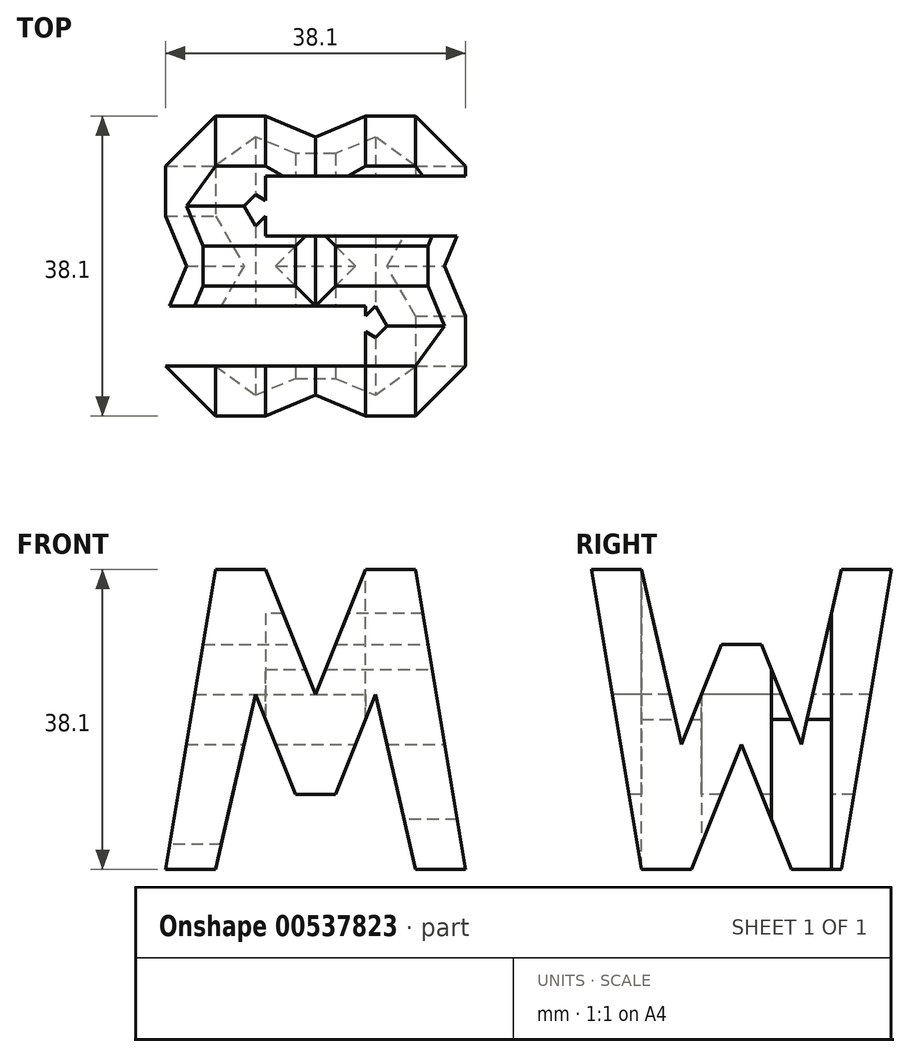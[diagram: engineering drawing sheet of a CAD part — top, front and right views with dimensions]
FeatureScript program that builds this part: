
annotation { "Feature Type Name" : "Feature", "Feature Type Description" : "" }
export const myFeature = defineFeature(function(context is Context, id is Id, definition is map)
    precondition{}
    {
        {
            var Q0;
            Q0=qCreatedBy(makeId("Front.planeOp"),FACE);
            var sketch = newSketch(context, id + "F0", { "sketchPlane" : qUnion([Q0])});
            skLineSegment(sketch, "E0", {"start": v(0, 0) * mm, "end": v(0, 38.1) * mm});
            skLineSegment(sketch, "E1", {"start": v(0, 38.1) * mm, "end": v(38.1, 38.1) * mm});
            skLineSegment(sketch, "E2", {"start": v(38.1, 38.1) * mm, "end": v(38.1, 0) * mm});
            skLineSegment(sketch, "E3", {"start": v(38.1, 0) * mm, "end": v(0, 0) * mm});
            skSolve(sketch);
        }
        {
            var Q0;
            Q0 = qSketchRegion(id + "F0", true);
            extrude(context, id + "F1", {"entities" : qUnion([Q0]), "depth" : 38.1 * mm, "offsetDistance" : 25.4 * mm});
        }
        {
            var Q0;
            Q0=qCreatedBy(makeId("Front.planeOp"),FACE);
            cPlane(context, id + "F2", {"entities" : qUnion([Q0]), "cplaneType" : CPlaneType.OFFSET, "offset" : 38.1 * mm, "width" : 152.4 * mm, "height" : 152.4 * mm});
        }
        {
            var Q0;
            Q0=qCreatedBy(makeId("Right.planeOp"),FACE);
            cPlane(context, id + "F3", {"entities" : qUnion([Q0]), "cplaneType" : CPlaneType.OFFSET, "offset" : 38.1 * mm, "width" : 152.4 * mm, "height" : 152.4 * mm});
        }
        {
            var Q0;
            Q0=qCreatedBy(makeId("Top.planeOp"),FACE);
            cPlane(context, id + "F4", {"entities" : qUnion([Q0]), "cplaneType" : CPlaneType.OFFSET, "offset" : 38.1 * mm, "width" : 152.4 * mm, "height" : 152.4 * mm});
        }
        {
            var Q0;
            Q0=qCreatedBy(id+"F3.planeOp",FACE);
            var sketch = newSketch(context, id + "F5", { "sketchPlane" : qUnion([Q0])});
            skLineSegment(sketch, "E4.bottom", {"start": v(0, 0) * mm, "end": v(-38.1, 0) * mm});
            skLineSegment(sketch, "E4.top", {"start": v(0, 38.1) * mm, "end": v(-38.1, 38.1) * mm});
            skLineSegment(sketch, "E4.left", {"start": v(0, 0) * mm, "end": v(0, 38.1) * mm});
            skLineSegment(sketch, "E4.right", {"start": v(-38.1, 0) * mm, "end": v(-38.1, 38.1) * mm});
            skLineSegment(sketch, "E5", {"start": v(-38.1, 38.1) * mm, "end": v(-31.75, 0) * mm});
            skLineSegment(sketch, "E6", {"start": v(-31.75, 0) * mm, "end": v(-25.4, 0) * mm});
            skLineSegment(sketch, "E7", {"start": v(-25.4, 0) * mm, "end": v(-19.05, 15.87) * mm});
            skLineSegment(sketch, "E8", {"start": v(-19.05, 15.87) * mm, "end": v(-12.7, 0) * mm});
            skLineSegment(sketch, "E9", {"start": v(-12.7, 0) * mm, "end": v(-6.35, 0) * mm});
            skLineSegment(sketch, "E10", {"start": v(-6.35, 0) * mm, "end": v(0, 38.1) * mm});
            skLineSegment(sketch, "E11", {"start": v(-6.35, 38.1) * mm, "end": v(-11.43, 15.87) * mm});
            skLineSegment(sketch, "E12", {"start": v(-11.43, 15.87) * mm, "end": v(-16.51, 28.57) * mm});
            skLineSegment(sketch, "E13", {"start": v(-16.51, 28.57) * mm, "end": v(-21.6, 28.57) * mm});
            skLineSegment(sketch, "E14", {"start": v(-21.6, 28.57) * mm, "end": v(-26.67, 15.87) * mm});
            skLineSegment(sketch, "E15", {"start": v(-26.67, 15.87) * mm, "end": v(-31.75, 38.1) * mm});
            skLineSegment(sketch, "E16", {"start": v(-31.75, 38.1) * mm, "end": v(-38.1, 38.1) * mm});
            skSolve(sketch);
        }
        {
            var Q0;
            {var subQ0=sQuery(id+"F5.wireOp",EDGE,"E4.right");Q0=makeQuery(id+"F5.imprint","IMPRINT",FACE,{"disambiguationData":[TD([[makeQuery(id+"F5.imprint","IMPRINT",EDGE,{"derivedFrom":subQ0}),-1.0]])]});}
            var Q1;
            {var subQ0=sQuery(id+"F5.wireOp",EDGE,"E7");Q1=makeQuery(id+"F5.imprint","IMPRINT",FACE,{"disambiguationData":[TD([[makeQuery(id+"F5.imprint","IMPRINT",EDGE,{"derivedFrom":subQ0}),-1.0]])]});}
            var Q2;
            {var subQ2=sQuery(id+"F5.wireOp",EDGE,"E11");Q2=makeQuery(id+"F5.imprint","IMPRINT",FACE,{"disambiguationData":[TD([[makeQuery(id+"F5.imprint","IMPRINT",EDGE,{"derivedFrom":subQ2}),-1.0]])]});}
            var Q3;
            {var subQ0=sQuery(id+"F5.wireOp",EDGE,"E4.left");Q3=makeQuery(id+"F5.imprint","IMPRINT",FACE,{"disambiguationData":[TD([[makeQuery(id+"F5.imprint","IMPRINT",EDGE,{"derivedFrom":subQ0}),1.0]])]});}
            extrude(context, id + "F6", {"entities" : qUnion([Q0, Q1, Q2, Q3]), "operationType" : NewBodyOperationType.REMOVE, "oppositeDirection" : true, "depth" : 38.1 * mm, "offsetDistance" : 25.4 * mm});
        }
        {
            var Q0;
            Q0=qCreatedBy(id+"F2.planeOp",FACE);
            var sketch = newSketch(context, id + "F7", { "sketchPlane" : qUnion([Q0])});
            skLineSegment(sketch, "E17", {"start": v(0, 0) * mm, "end": v(6.35, 38.1) * mm});
            skLineSegment(sketch, "E18", {"start": v(12.7, 38.1) * mm, "end": v(19.05, 22.23) * mm});
            skLineSegment(sketch, "E19", {"start": v(25.4, 38.1) * mm, "end": v(19.05, 22.23) * mm});
            skLineSegment(sketch, "E20", {"start": v(38.1, 0) * mm, "end": v(31.75, 38.1) * mm});
            skLineSegment(sketch, "E21", {"start": v(6.35, 0) * mm, "end": v(11.43, 22.23) * mm});
            skLineSegment(sketch, "E22", {"start": v(11.43, 22.23) * mm, "end": v(16.51, 9.53) * mm});
            skLineSegment(sketch, "E23", {"start": v(16.51, 9.53) * mm, "end": v(21.59, 9.53) * mm});
            skLineSegment(sketch, "E24", {"start": v(21.59, 9.53) * mm, "end": v(26.67, 22.23) * mm});
            skLineSegment(sketch, "E25", {"start": v(26.67, 22.23) * mm, "end": v(31.75, 0) * mm});
            skLineSegment(sketch, "E26.bottom", {"start": v(0, 0) * mm, "end": v(38.1, 0) * mm});
            skLineSegment(sketch, "E26.top", {"start": v(0, 38.1) * mm, "end": v(38.1, 38.1) * mm});
            skLineSegment(sketch, "E26.left", {"start": v(0, 0) * mm, "end": v(0, 38.1) * mm});
            skLineSegment(sketch, "E26.right", {"start": v(38.1, 0) * mm, "end": v(38.1, 38.1) * mm});
            skSolve(sketch);
        }
        {
            var Q0;
            {var subQ0=sQuery(id+"F7.wireOp",EDGE,"E18");Q0=makeQuery(id+"F7.imprint","IMPRINT",FACE,{"disambiguationData":[TD([[makeQuery(id+"F7.imprint","IMPRINT",EDGE,{"derivedFrom":subQ0}),1.0]])]});}
            var Q1;
            {var subQ0=sQuery(id+"F7.wireOp",EDGE,"E17");Q1=makeQuery(id+"F7.imprint","IMPRINT",FACE,{"disambiguationData":[TD([[makeQuery(id+"F7.imprint","IMPRINT",EDGE,{"derivedFrom":subQ0}),1.0]])]});}
            var Q2;
            {var subQ0=sQuery(id+"F7.wireOp",EDGE,"E21");Q2=makeQuery(id+"F7.imprint","IMPRINT",FACE,{"disambiguationData":[TD([[makeQuery(id+"F7.imprint","IMPRINT",EDGE,{"derivedFrom":subQ0}),-1.0]])]});}
            var Q3;
            {var subQ0=sQuery(id+"F7.wireOp",EDGE,"E20");Q3=makeQuery(id+"F7.imprint","IMPRINT",FACE,{"disambiguationData":[TD([[makeQuery(id+"F7.imprint","IMPRINT",EDGE,{"derivedFrom":subQ0}),-1.0]])]});}
            extrude(context, id + "F8", {"entities" : qUnion([Q0, Q1, Q2, Q3]), "operationType" : NewBodyOperationType.REMOVE, "oppositeDirection" : true, "depth" : 38.1 * mm, "offsetDistance" : 25.4 * mm});
        }
        {
            var Q0;
            Q0=qCreatedBy(id+"F4.planeOp",FACE);
            var sketch = newSketch(context, id + "F9", { "sketchPlane" : qUnion([Q0])});
            skLineSegment(sketch, "E27", {"start": v(0, 0) * mm, "end": v(38.1, 0) * mm});
            skLineSegment(sketch, "E28", {"start": v(38.1, 0) * mm, "end": v(38.1, -38.1) * mm});
            skLineSegment(sketch, "E29", {"start": v(38.1, -38.1) * mm, "end": v(0, -38.1) * mm});
            skLineSegment(sketch, "E30", {"start": v(0, -38.1) * mm, "end": v(0, 0) * mm});
            skLineSegment(sketch, "E31", {"start": v(38.1, -7.62) * mm, "end": v(12.7, -7.62) * mm});
            skLineSegment(sketch, "E32", {"start": v(12.7, -7.62) * mm, "end": v(12.7, -15.24) * mm});
            skLineSegment(sketch, "E33", {"start": v(12.7, -15.24) * mm, "end": v(38.1, -15.24) * mm});
            skLineSegment(sketch, "E34", {"start": v(0, -24.13) * mm, "end": v(25.4, -24.13) * mm});
            skLineSegment(sketch, "E35", {"start": v(25.4, -24.13) * mm, "end": v(25.4, -31.75) * mm});
            skLineSegment(sketch, "E36", {"start": v(25.4, -31.75) * mm, "end": v(0, -31.75) * mm});
            skSolve(sketch);
        }
        {
            var Q0;
            {var subQ0=sQuery(id+"F9.wireOp",EDGE,"E31");Q0=makeQuery(id+"F9.imprint","IMPRINT",FACE,{"disambiguationData":[TD([[makeQuery(id+"F9.imprint","IMPRINT",EDGE,{"derivedFrom":subQ0}),1.0]])]});}
            var Q1;
            {var subQ0=sQuery(id+"F9.wireOp",EDGE,"E34");Q1=makeQuery(id+"F9.imprint","IMPRINT",FACE,{"disambiguationData":[TD([[makeQuery(id+"F9.imprint","IMPRINT",EDGE,{"derivedFrom":subQ0}),-1.0]])]});}
            extrude(context, id + "F10", {"entities" : qUnion([Q0, Q1]), "operationType" : NewBodyOperationType.REMOVE, "oppositeDirection" : true, "depth" : 38.1 * mm, "offsetDistance" : 25.4 * mm});
        }
    });
